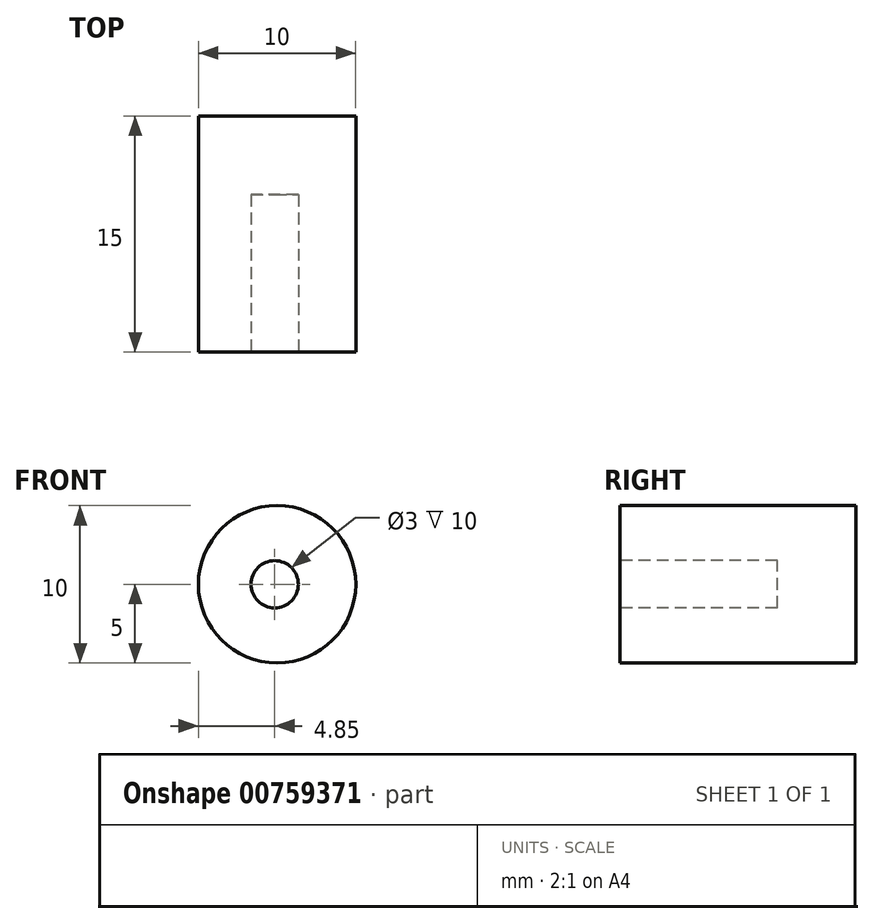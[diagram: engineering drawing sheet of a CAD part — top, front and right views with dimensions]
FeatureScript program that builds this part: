
annotation { "Feature Type Name" : "Feature", "Feature Type Description" : "" }
export const myFeature = defineFeature(function(context is Context, id is Id, definition is map)
    precondition{}
    {
        {
            var Q0;
            Q0=qCreatedBy(makeId("Front.planeOp"),FACE);
            var sketch = newSketch(context, id + "F0", { "sketchPlane" : qUnion([Q0])});
            skCircle(sketch, "E0", {"center": v(0, 0) * mm, "radius": 1.5 * mm});
            skCircle(sketch, "E1", {"center": v(0.15, 0) * mm, "radius": 5 * mm});
            skSolve(sketch);
        }
        {
            var Q0;
            Q0=makeQuery(id+"F0.imprint","IMPRINT",FACE,{"disambiguationData":[TD([[makeQuery(id+"F0.imprint","IMPRINT",EDGE,{"derivedFrom":sQuery(id+"F0.wireOp",EDGE,"E0")}),-1.0]])]});
            var Q1;
            Q1=makeQuery(id+"F0.imprint","IMPRINT",FACE,{"disambiguationData":[TD([[makeQuery(id+"F0.imprint","IMPRINT",EDGE,{"derivedFrom":sQuery(id+"F0.wireOp",EDGE,"E0")}),1.0]])]});
            extrude(context, id + "F1", {"entities" : qUnion([Q0, Q1]), "oppositeDirection" : true, "depth" : 15 * mm, "offsetDistance" : 25 * mm});
        }
        {
            var Q0;
            Q0=makeQuery(id+"F0.imprint","IMPRINT",FACE,{"disambiguationData":[TD([[makeQuery(id+"F0.imprint","IMPRINT",EDGE,{"derivedFrom":sQuery(id+"F0.wireOp",EDGE,"E0")}),1.0]])]});
            extrude(context, id + "F2", {"entities" : qUnion([Q0]), "operationType" : NewBodyOperationType.REMOVE, "oppositeDirection" : true, "depth" : 10 * mm, "offsetDistance" : 25 * mm});
        }
    });
